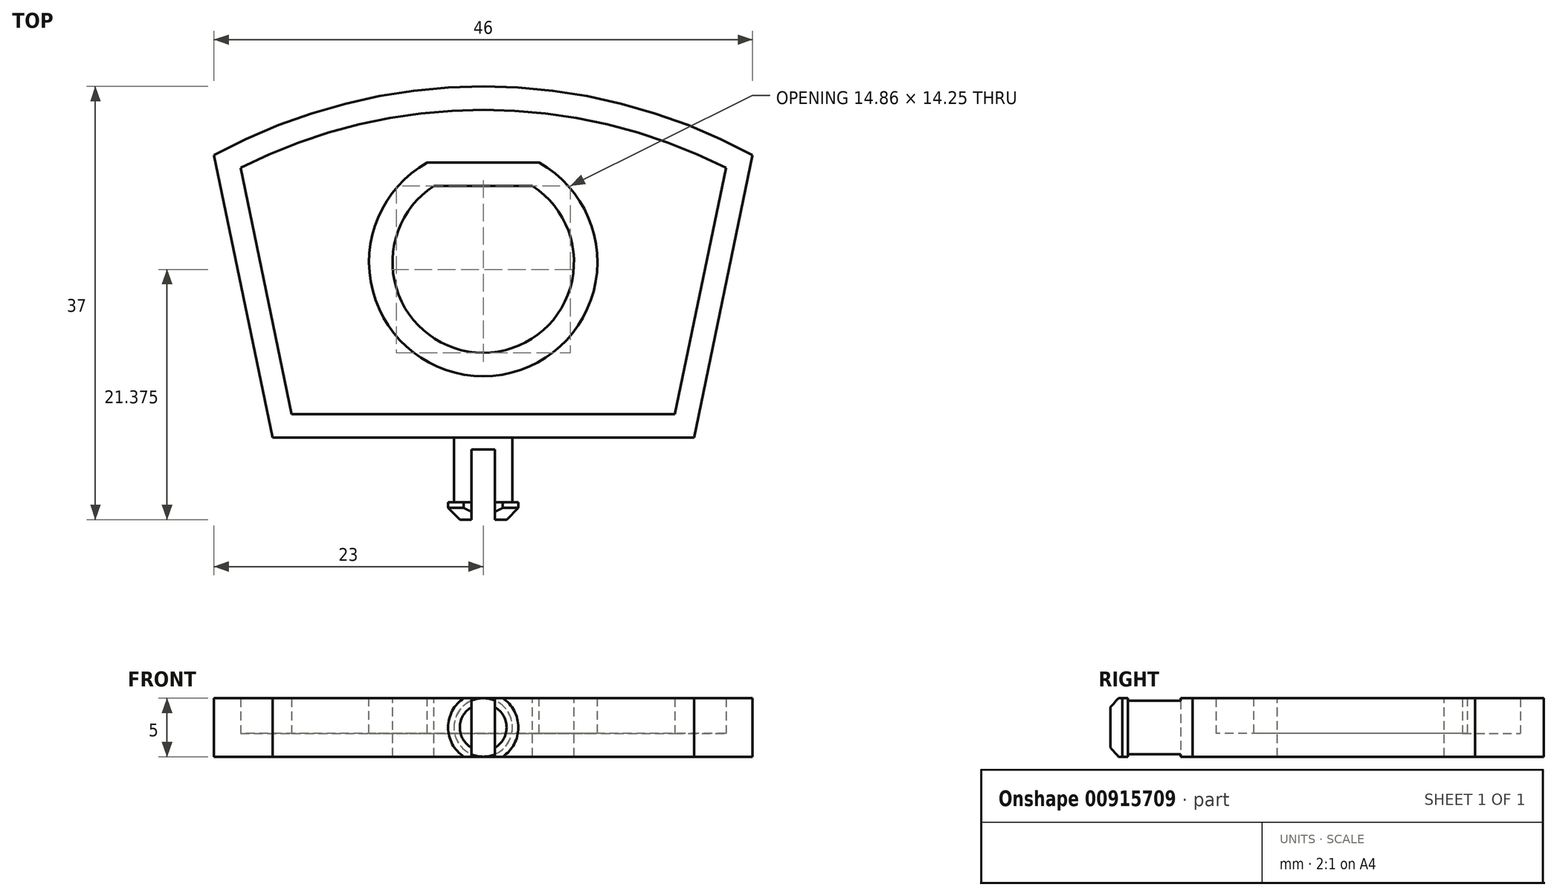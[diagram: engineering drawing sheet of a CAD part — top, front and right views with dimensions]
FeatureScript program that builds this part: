
annotation { "Feature Type Name" : "Feature", "Feature Type Description" : "" }
export const myFeature = defineFeature(function(context is Context, id is Id, definition is map)
    precondition{}
    {
        {
            var Q0;
            Q0=qCreatedBy(makeId("Top.planeOp"),FACE);
            var sketch = newSketch(context, id + "F0", { "sketchPlane" : qUnion([Q0])});
            skLineSegment(sketch, "E0", {"start": v(-23, 24.13) * mm, "end": v(-18, 0) * mm});
            skLineSegment(sketch, "E1", {"start": v(-18, 0) * mm, "end": v(0, 0) * mm});
            skLineSegment(sketch, "E2", {"start": v(0, 0) * mm, "end": v(18, 0) * mm});
            skLineSegment(sketch, "E3", {"start": v(18, 0) * mm, "end": v(23, 24.13) * mm});
            skArc(sketch, "E4", {"start": v(23, 24.13) * mm, "mid": v(0, 30) * mm, "end": v(-23, 24.13) * mm});
            skSolve(sketch);
        }
        {
            var Q0;
            Q0 = qSketchRegion(id + "F0", true);
            extrude(context, id + "F1", {"entities" : qUnion([Q0]), "endBound" : BoundingType.SYMMETRIC, "depth" : 5 * mm, "offsetDistance" : 25 * mm});
        }
        {
            var Q0;
            Q0=makeQuery(id+"F1.opExtrude","CAP_FACE",FACE,{"disambiguationData":[OSD([sQuery(id+"F0.wireOp",EDGE,"E0"),sQuery(id+"F0.wireOp",EDGE,"E1"),sQuery(id+"F0.wireOp",EDGE,"E2"),sQuery(id+"F0.wireOp",EDGE,"E3"),sQuery(id+"F0.wireOp",EDGE,"E4")])],"isStart":false});
            var sketch = newSketch(context, id + "F2", { "sketchPlane" : qUnion([Q0])});
            skLineSegment(sketch, "E5", {"start": v(-4.22, 21.5) * mm, "end": v(4.22, 21.5) * mm});
            skArc(sketch, "E6", {"start": v(-4.22, 21.5) * mm, "mid": v(0, 7.25) * mm, "end": v(4.22, 21.5) * mm});
            skSolve(sketch);
        }
        {
            var Q0;
            Q0 = qSketchRegion(id + "F2", true);
            extrude(context, id + "F3", {"entities" : qUnion([Q0]), "operationType" : NewBodyOperationType.REMOVE, "endBound" : BoundingType.UP_TO_NEXT, "oppositeDirection" : true, "depth" : 25 * mm, "offsetDistance" : 25 * mm});
        }
        {
            var Q0;
            Q0=makeQuery(id+"F1.opExtrude","CAP_FACE",FACE,{"disambiguationData":[OSD([sQuery(id+"F0.wireOp",EDGE,"E0"),sQuery(id+"F0.wireOp",EDGE,"E1"),sQuery(id+"F0.wireOp",EDGE,"E2"),sQuery(id+"F0.wireOp",EDGE,"E3"),sQuery(id+"F0.wireOp",EDGE,"E4")])],"isStart":false});
            shell(context, id + "F4", {"entities" : qUnion([Q0]), "thickness" : 2 * mm});
        }
        {
            var Q0;
            Q0=qCreatedBy(makeId("Right.planeOp"),FACE);
            var sketch = newSketch(context, id + "F5", { "sketchPlane" : qUnion([Q0])});
            skLineSegment(sketch, "E7", {"start": v(0, 0) * mm, "end": v(-7, 0) * mm});
            skLineSegment(sketch, "E8", {"start": v(-7, 0) * mm, "end": v(-7, 3) * mm});
            skLineSegment(sketch, "E9", {"start": v(-7, 3) * mm, "end": v(-5.5, 3) * mm});
            skLineSegment(sketch, "E10", {"start": v(-5.5, 3) * mm, "end": v(-5.5, 2.5) * mm});
            skLineSegment(sketch, "E11", {"start": v(-5.5, 2.5) * mm, "end": v(0, 2.5) * mm});
            skLineSegment(sketch, "E12", {"start": v(0, 0) * mm, "end": v(0, 2.5) * mm});
            skSolve(sketch);
        }
        {
            var Q0;
            Q0 = qSketchRegion(id + "F5", true);
            var Q1;
            Q1=sQuery(id+"F5.wireOp",EDGE,"E7");
            revolve(context, id + "F6", {"operationType" : NewBodyOperationType.ADD, "surfaceOperationType" : NewSurfaceOperationType.NEW, "entities" : qUnion([Q0]), "axis" : qUnion([Q1]), "revolveType" : RevolveType.FULL});
        }
        {
            var Q0;
            Q0=makeQuery(id+"F6.opRevolve","SWEPT_EDGE",EDGE,{"disambiguationData":[OSD([sQuery(id+"F5.wireOp",EDGE,"E8"),sQuery(id+"F5.wireOp",EDGE,"E9")])]});
            chamfer(context, id + "F7", {"entities" : qUnion([Q0]), "width" : 1 * mm, "tangentPropagation" : true});
        }
        {
            var Q0;
            Q0=makeQuery(id+"F6.opRevolve","SWEPT_FACE",FACE,{"disambiguationData":[OSD([sQuery(id+"F5.wireOp",EDGE,"E8")])]});
            var sketch = newSketch(context, id + "F8", { "sketchPlane" : qUnion([Q0])});
            skLineSegment(sketch, "E13.bottom", {"start": v(-25, 2.5) * mm, "end": v(25, 2.5) * mm});
            skLineSegment(sketch, "E13.top", {"start": v(-25, -2.5) * mm, "end": v(25, -2.5) * mm});
            skLineSegment(sketch, "E13.left", {"start": v(-25, 2.5) * mm, "end": v(-25, -2.5) * mm});
            skLineSegment(sketch, "E13.right", {"start": v(25, 2.5) * mm, "end": v(25, -2.5) * mm});
            skSolve(sketch);
        }
        {
            var Q0;
            Q0 = qSketchRegion(id + "F8", true);
            extrude(context, id + "F9", {"entities" : qUnion([Q0]), "operationType" : NewBodyOperationType.INTERSECT, "endBound" : BoundingType.THROUGH_ALL, "oppositeDirection" : true, "depth" : 25 * mm, "offsetDistance" : 25 * mm});
        }
        {
            var Q0;
            Q0=makeQuery(id+"F6.opRevolve","SWEPT_FACE",FACE,{"disambiguationData":[OSD([sQuery(id+"F5.wireOp",EDGE,"E8")])]});
            var sketch = newSketch(context, id + "F10", { "sketchPlane" : qUnion([Q0])});
            skLineSegment(sketch, "E14.bottom", {"start": v(-1, 5.08) * mm, "end": v(1, 5.08) * mm});
            skLineSegment(sketch, "E14.top", {"start": v(-1, -5.83) * mm, "end": v(1, -5.83) * mm});
            skLineSegment(sketch, "E14.left", {"start": v(-1, 5.08) * mm, "end": v(-1, -5.83) * mm});
            skLineSegment(sketch, "E14.right", {"start": v(1, 5.08) * mm, "end": v(1, -5.83) * mm});
            skSolve(sketch);
        }
        {
            var Q0;
            Q0 = qSketchRegion(id + "F10", true);
            extrude(context, id + "F11", {"entities" : qUnion([Q0]), "operationType" : NewBodyOperationType.REMOVE, "oppositeDirection" : true, "depth" : 6 * mm, "offsetDistance" : 25 * mm});
        }
    });
